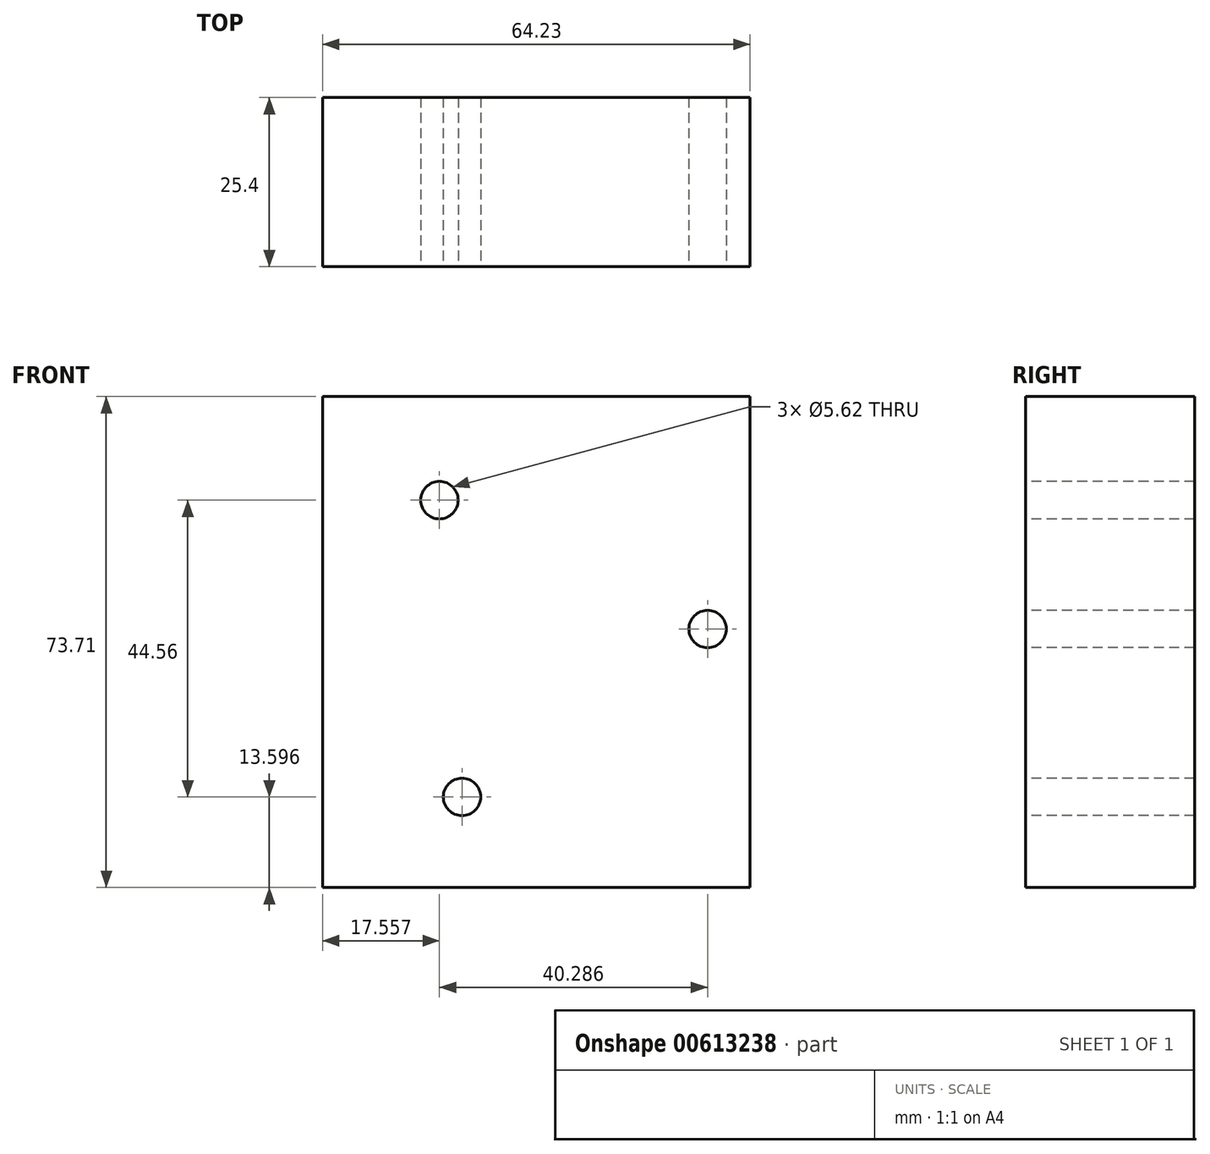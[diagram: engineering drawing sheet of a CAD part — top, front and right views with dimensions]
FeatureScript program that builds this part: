
annotation { "Feature Type Name" : "Feature", "Feature Type Description" : "" }
export const myFeature = defineFeature(function(context is Context, id is Id, definition is map)
    precondition{}
    {
        {
            var Q0;
            Q0=qCreatedBy(makeId("Front.planeOp"),FACE);
            var sketch = newSketch(context, id + "F0", { "sketchPlane" : qUnion([Q0])});
            skLineSegment(sketch, "E0.bottom", {"start": v(-68.34, 10.53) * mm, "end": v(-4.1, 10.53) * mm});
            skLineSegment(sketch, "E0.top", {"start": v(-68.34, 84.24) * mm, "end": v(-4.1, 84.24) * mm});
            skLineSegment(sketch, "E0.left", {"start": v(-68.34, 10.53) * mm, "end": v(-68.34, 84.24) * mm});
            skLineSegment(sketch, "E0.right", {"start": v(-4.1, 10.53) * mm, "end": v(-4.1, 84.24) * mm});
            skSolve(sketch);
        }
        {
            var Q0;
            Q0 = qSketchRegion(id + "F0", true);
            extrude(context, id + "F1", {"entities" : qUnion([Q0]), "endBound" : BoundingType.SYMMETRIC, "depth" : 25.4 * mm, "offsetDistance" : 25.4 * mm});
        }
        {
            var Q0;
            Q0=makeQuery(id+"F1.opExtrude","SWEPT_FACE",FACE,{"disambiguationData":[OSD([sQuery(id+"F0.wireOp",EDGE,"E0.right")])]});
            var Q1;
            Q1=makeQuery(id+"F1.opExtrude","SWEPT_FACE",FACE,{"disambiguationData":[OSD([sQuery(id+"F0.wireOp",EDGE,"E0.left")])]});
            cPlane(context, id + "F2", {"entities" : qUnion([Q0, Q1]), "cplaneType" : CPlaneType.MID_PLANE, "offset" : 25.4 * mm, "width" : 152.4 * mm, "height" : 152.4 * mm});
        }
        {
            var Q0;
            Q0=makeQuery(id+"F1.opExtrude","SWEPT_FACE",FACE,{"disambiguationData":[OSD([sQuery(id+"F0.wireOp",EDGE,"E0.top")])]});
            var Q1;
            Q1=makeQuery(id+"F1.opExtrude","SWEPT_FACE",FACE,{"disambiguationData":[OSD([sQuery(id+"F0.wireOp",EDGE,"E0.bottom")])]});
            cPlane(context, id + "F3", {"entities" : qUnion([Q0, Q1]), "cplaneType" : CPlaneType.MID_PLANE, "offset" : 25.4 * mm, "width" : 152.4 * mm, "height" : 152.4 * mm});
        }
        {
            var Q0;
            Q0=makeQuery(id+"F1.opExtrude","CAP_FACE",FACE,{"disambiguationData":[OSD([sQuery(id+"F0.wireOp",EDGE,"E0.bottom"),sQuery(id+"F0.wireOp",EDGE,"E0.top"),sQuery(id+"F0.wireOp",EDGE,"E0.left"),sQuery(id+"F0.wireOp",EDGE,"E0.right")])],"isStart":false});
            var sketch = newSketch(context, id + "F4", { "sketchPlane" : qUnion([Q0])});
            skCircle(sketch, "E1", {"center": v(-50.78, 68.69) * mm, "radius": 2.8 * mm});
            skPoint(sketch, "E2", {"position": v(-36.22, 47.39) * mm});
            skCircle(sketch, "E3.1.0", {"center": v(-47.4, 24.13) * mm, "radius": 2.8 * mm});
            skCircle(sketch, "E3.2.0", {"center": v(-10.5, 49.34) * mm, "radius": 2.8 * mm});
            skSolve(sketch);
        }
        {
            var Q0;
            Q0 = qSketchRegion(id + "F4", true);
            extrude(context, id + "F5", {"entities" : qUnion([Q0]), "operationType" : NewBodyOperationType.REMOVE, "endBound" : BoundingType.THROUGH_ALL, "oppositeDirection" : true, "depth" : 25.4 * mm, "offsetDistance" : 25.4 * mm});
        }
        {
            var Q0;
            Q0=qCreatedBy(id+"F2.planeOp",FACE);
            var sketch = newSketch(context, id + "F6", { "sketchPlane" : qUnion([Q0])});
            skLineSegment(sketch, "E4", {"start": v(-12.7, 47.39) * mm, "end": v(12.7, 47.39) * mm});
            skSolve(sketch);
        }
    });
